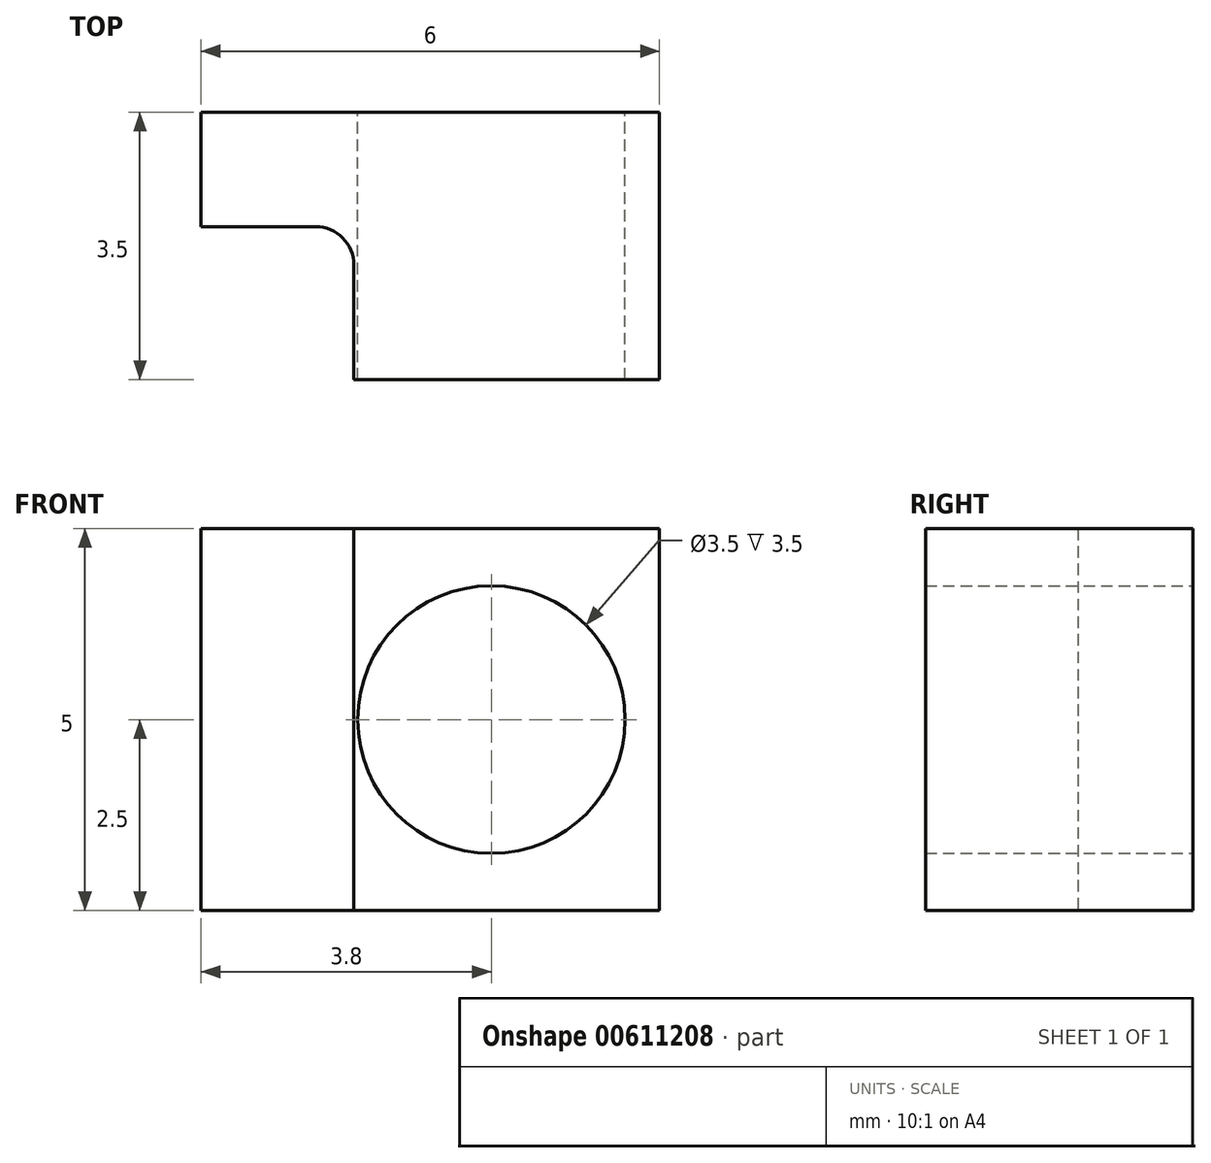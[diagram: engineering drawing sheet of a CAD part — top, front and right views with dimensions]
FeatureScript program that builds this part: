
annotation { "Feature Type Name" : "Feature", "Feature Type Description" : "" }
export const myFeature = defineFeature(function(context is Context, id is Id, definition is map)
    precondition{}
    {
        {
            var Q0;
            Q0=qCreatedBy(makeId("Top.planeOp"),FACE);
            var sketch = newSketch(context, id + "F0", { "sketchPlane" : qUnion([Q0])});
            skLineSegment(sketch, "E0", {"start": v(0, 0) * mm, "end": v(0, 3.5) * mm});
            skLineSegment(sketch, "E1", {"start": v(0, 0) * mm, "end": v(-4, 0) * mm});
            skLineSegment(sketch, "E2", {"start": v(0, 3.5) * mm, "end": v(-6, 3.5) * mm});
            skLineSegment(sketch, "E3", {"start": v(-6, 3.5) * mm, "end": v(-6, 2) * mm});
            skLineSegment(sketch, "E4", {"start": v(-6, 2) * mm, "end": v(-4.5, 2) * mm});
            skLineSegment(sketch, "E5", {"start": v(-4, 0) * mm, "end": v(-4, 1.5) * mm});
            skArc(sketch, "E6", {"start": v(-4, 1.5) * mm, "mid": v(-4.15, 1.85) * mm, "end": v(-4.5, 2) * mm});
            skSolve(sketch);
        }
        {
            var Q0;
            Q0=makeQuery(id+"F0.imprint","IMPRINT",FACE,{"disambiguationData":[TD([[makeQuery(id+"F0.imprint","IMPRINT",EDGE,{"derivedFrom":sQuery(id+"F0.wireOp",EDGE,"E0")}),1.0]])]});
            extrude(context, id + "F1", {"entities" : qUnion([Q0]), "depth" : 5 * mm, "offsetDistance" : 25 * mm});
        }
        {
            var Q0;
            Q0=makeQuery(id+"F1.opExtrude","SWEPT_FACE",FACE,{"disambiguationData":[OSD([sQuery(id+"F0.wireOp",EDGE,"E2")])]});
            var sketch = newSketch(context, id + "F2", { "sketchPlane" : qUnion([Q0])});
            skPoint(sketch, "E7", {"position": v(2.2, 2.5) * mm});
            skPoint(sketch, "E7.positionSnap0", {"position": v(0, 2.5) * mm});
            skCircle(sketch, "E8", {"center": v(2.2, 2.5) * mm, "radius": 1.75 * mm});
            skSolve(sketch);
        }
        {
            var Q0;
            Q0=makeQuery(id+"F2.imprint","IMPRINT",FACE,{"disambiguationData":[TD([[makeQuery(id+"F2.imprint","IMPRINT",EDGE,{"derivedFrom":sQuery(id+"F2.wireOp",EDGE,"E8")}),1.0]])]});
            extrude(context, id + "F3", {"entities" : qUnion([Q0]), "operationType" : NewBodyOperationType.REMOVE, "oppositeDirection" : true, "depth" : 25 * mm, "offsetDistance" : 25 * mm});
        }
    });
